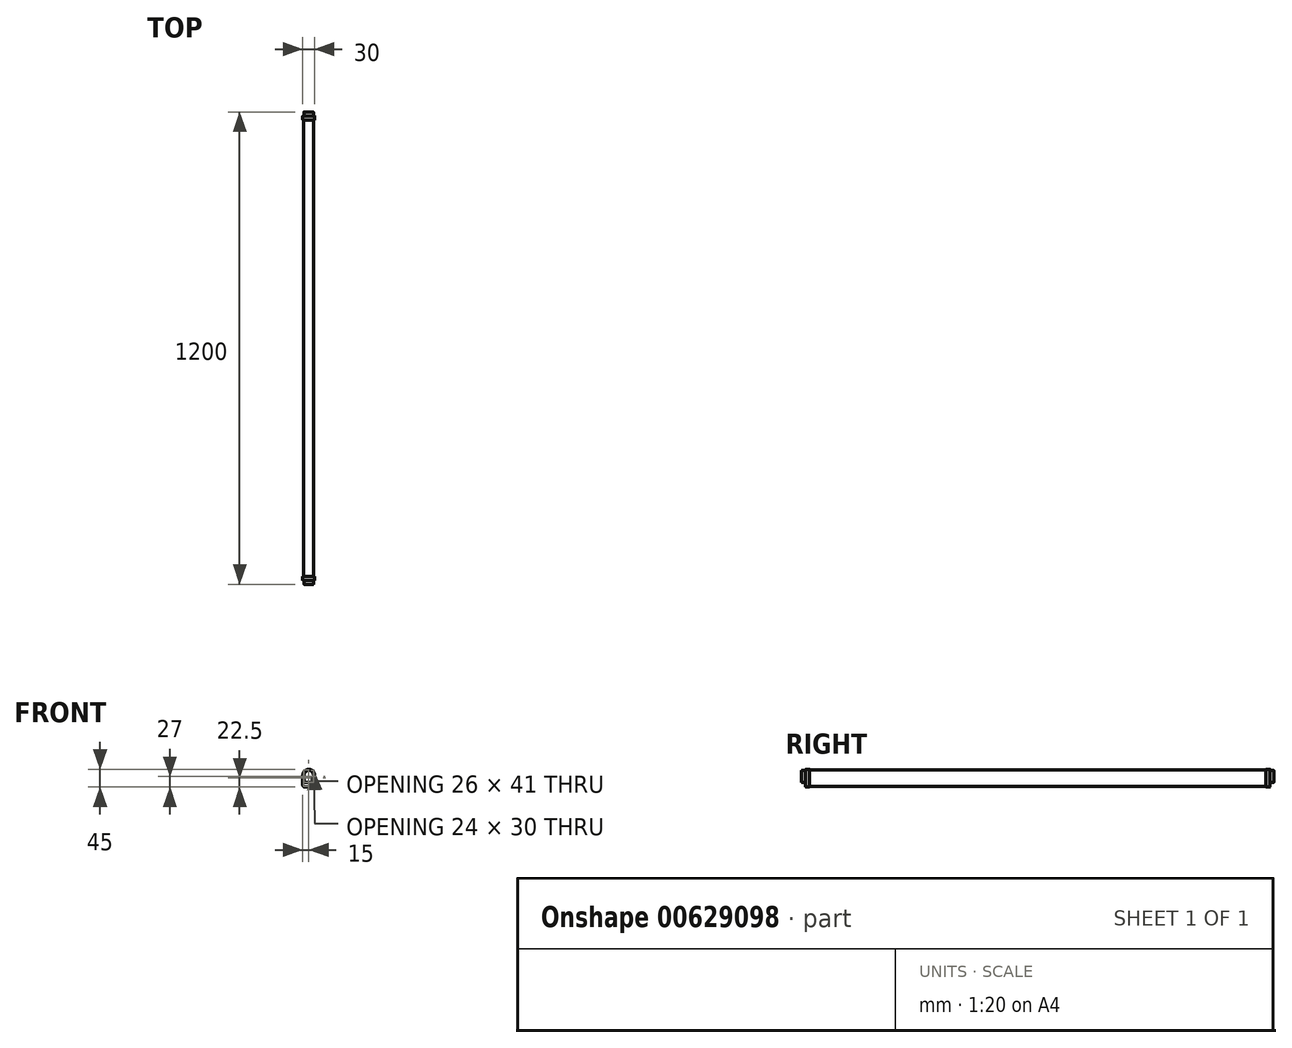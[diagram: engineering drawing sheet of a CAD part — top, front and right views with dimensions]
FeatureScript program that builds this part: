
annotation { "Feature Type Name" : "Feature", "Feature Type Description" : "" }
export const myFeature = defineFeature(function(context is Context, id is Id, definition is map)
    precondition{}
    {
        {
            var Q0;
            Q0=qCreatedBy(makeId("Front.planeOp"),FACE);
            var sketch = newSketch(context, id + "F0", { "sketchPlane" : qUnion([Q0])});
            skLineSegment(sketch, "E0.bottom", {"start": v(10, -22.5) * mm, "end": v(-10, -22.5) * mm});
            skLineSegment(sketch, "E0.top", {"start": v(0, 22.5) * mm, "end": v(0, 22.5) * mm});
            skLineSegment(sketch, "E0.left", {"start": v(15, -17.5) * mm, "end": v(15, 7.5) * mm});
            skLineSegment(sketch, "E0.right", {"start": v(-15, -17.5) * mm, "end": v(-15, 7.5) * mm});
            skPoint(sketch, "E0.middle", {"position": v(0, 0) * mm});
            skPoint(sketch, "E1.visualSharp", {"position": v(-15, 22.5) * mm});
            skArc(sketch, "E1.filletArc", {"start": v(0, 22.5) * mm, "mid": v(-10.6, 18.1) * mm, "end": v(-15, 7.5) * mm});
            skPoint(sketch, "E2.visualSharp", {"position": v(15, 22.5) * mm});
            skArc(sketch, "E2.filletArc", {"start": v(15, 7.5) * mm, "mid": v(10.6, 18.1) * mm, "end": v(0, 22.5) * mm});
            skPoint(sketch, "E3.visualSharp", {"position": v(-15, -22.5) * mm});
            skArc(sketch, "E3.filletArc", {"start": v(-15, -17.5) * mm, "mid": v(-13.54, -21.04) * mm, "end": v(-10, -22.5) * mm});
            skPoint(sketch, "E4.visualSharp", {"position": v(15, -22.5) * mm});
            skArc(sketch, "E4.filletArc", {"start": v(10, -22.5) * mm, "mid": v(13.54, -21.04) * mm, "end": v(15, -17.5) * mm});
            skArc(sketch, "E5.1", {"start": v(12, 7.5) * mm, "mid": v(8.49, 15.99) * mm, "end": v(0, 19.5) * mm});
            skArc(sketch, "E5.2", {"start": v(0, 19.5) * mm, "mid": v(-8.49, 15.99) * mm, "end": v(-12, 7.5) * mm});
            skPoint(sketch, "E6", {"position": v(0, -10.5) * mm});
            skLineSegment(sketch, "E7", {"start": v(0, -10.5) * mm, "end": v(12, -10.5) * mm});
            skLineSegment(sketch, "E8", {"start": v(0, -10.5) * mm, "end": v(-12, -10.5) * mm});
            skLineSegment(sketch, "E9", {"start": v(12, -10.5) * mm, "end": v(12, 7.5) * mm});
            skLineSegment(sketch, "E10", {"start": v(-12, -10.5) * mm, "end": v(-12, 7.5) * mm});
            skArc(sketch, "E11.0", {"start": v(13, 7.5) * mm, "mid": v(9.2, 16.7) * mm, "end": v(0, 20.5) * mm});
            skLineSegment(sketch, "E11.1", {"start": v(13, -17.5) * mm, "end": v(13, 7.5) * mm});
            skLineSegment(sketch, "E11.2", {"start": v(-13, -17.5) * mm, "end": v(-13, 7.5) * mm});
            skArc(sketch, "E11.3", {"start": v(-13, -17.5) * mm, "mid": v(-12.12, -19.62) * mm, "end": v(-10, -20.5) * mm});
            skLineSegment(sketch, "E11.4", {"start": v(10, -20.5) * mm, "end": v(-10, -20.5) * mm});
            skArc(sketch, "E11.5", {"start": v(0, 20.5) * mm, "mid": v(-9.2, 16.7) * mm, "end": v(-13, 7.5) * mm});
            skArc(sketch, "E11.6", {"start": v(10, -20.5) * mm, "mid": v(12.12, -19.62) * mm, "end": v(13, -17.5) * mm});
            skSolve(sketch);
        }
        {
            var Q0;
            Q0=makeQuery(id+"F0.imprint","IMPRINT",FACE,{"disambiguationData":[TD([[makeQuery(id+"F0.imprint","IMPRINT",EDGE,{"derivedFrom":sQuery(id+"F0.wireOp",EDGE,"E5.1")}),-1.0]])]});
            var Q1;
            Q1=makeQuery(id+"F0.imprint","IMPRINT",FACE,{"disambiguationData":[TD([[makeQuery(id+"F0.imprint","IMPRINT",EDGE,{"derivedFrom":sQuery(id+"F0.wireOp",EDGE,"E5.1")}),1.0]])]});
            extrude(context, id + "F1", {"entities" : qUnion([Q0, Q1]), "depth" : 580 * mm, "offsetDistance" : 25 * mm});
        }
        {
            var Q0;
            Q0=makeQuery(id+"F1.opExtrude","CAP_FACE",FACE,{"disambiguationData":[OSD([sQuery(id+"F0.wireOp",EDGE,"E11.0"),sQuery(id+"F0.wireOp",EDGE,"E11.1"),sQuery(id+"F0.wireOp",EDGE,"E11.2"),sQuery(id+"F0.wireOp",EDGE,"E11.3"),sQuery(id+"F0.wireOp",EDGE,"E11.4"),sQuery(id+"F0.wireOp",EDGE,"E11.5"),sQuery(id+"F0.wireOp",EDGE,"E11.6")])],"isStart":false});
            var sketch = newSketch(context, id + "F2", { "sketchPlane" : qUnion([Q0])});
            skLineSegment(sketch, "E12.0.0", {"start": v(15, -17.5) * mm, "end": v(15, 7.5) * mm});
            skArc(sketch, "E12.0.1", {"start": v(15, 7.5) * mm, "mid": v(10.6, 18.1) * mm, "end": v(0, 22.5) * mm});
            skArc(sketch, "E12.0.2", {"start": v(0, 22.5) * mm, "mid": v(-10.6, 18.1) * mm, "end": v(-15, 7.5) * mm});
            skLineSegment(sketch, "E12.0.3", {"start": v(-15, 7.5) * mm, "end": v(-15, -17.5) * mm});
            skArc(sketch, "E12.0.4", {"start": v(-15, -17.5) * mm, "mid": v(-13.54, -21.04) * mm, "end": v(-10, -22.5) * mm});
            skLineSegment(sketch, "E12.0.5", {"start": v(-10, -22.5) * mm, "end": v(10, -22.5) * mm});
            skArc(sketch, "E12.0.6", {"start": v(10, -22.5) * mm, "mid": v(13.54, -21.04) * mm, "end": v(15, -17.5) * mm});
            skSolve(sketch);
        }
        {
            var Q0;
            Q0=qSketchRegion(id+"F2",true);
            extrude(context, id + "F3", {"entities" : qUnion([Q0]), "depth" : 10 * mm, "offsetDistance" : 25 * mm});
        }
        {
            var Q0;
            Q0=makeQuery(id+"F3.opExtrude","CAP_FACE",FACE,{"disambiguationData":[OSD([sQuery(id+"F2.wireOp",EDGE,"E12.0.0"),sQuery(id+"F2.wireOp",EDGE,"E12.0.1"),sQuery(id+"F2.wireOp",EDGE,"E12.0.2"),sQuery(id+"F2.wireOp",EDGE,"E12.0.3"),sQuery(id+"F2.wireOp",EDGE,"E12.0.4"),sQuery(id+"F2.wireOp",EDGE,"E12.0.5"),sQuery(id+"F2.wireOp",EDGE,"E12.0.6")])],"isStart":false});
            var sketch = newSketch(context, id + "F4", { "sketchPlane" : qUnion([Q0])});
            skLineSegment(sketch, "E13.0", {"start": v(-12, -10.5) * mm, "end": v(-12, 7.5) * mm});
            skArc(sketch, "E13.1", {"start": v(0, 19.5) * mm, "mid": v(-8.49, 15.99) * mm, "end": v(-12, 7.5) * mm});
            skArc(sketch, "E13.2", {"start": v(12, 7.5) * mm, "mid": v(8.49, 15.99) * mm, "end": v(0, 19.5) * mm});
            skLineSegment(sketch, "E13.3", {"start": v(12, -10.5) * mm, "end": v(12, 7.5) * mm});
            skLineSegment(sketch, "E13.4", {"start": v(0, -10.5) * mm, "end": v(12, -10.5) * mm});
            skLineSegment(sketch, "E13.5", {"start": v(0, -10.5) * mm, "end": v(-12, -10.5) * mm});
            skSolve(sketch);
        }
        {
            var Q0;
            Q0=qSketchRegion(id+"F4",true);
            extrude(context, id + "F5", {"entities" : qUnion([Q0]), "operationType" : NewBodyOperationType.ADD, "depth" : 10 * mm, "offsetDistance" : 25 * mm});
        }
        {
            var Q0;
            Q0=makeQuery(id+"F5.opExtrude","CAP_EDGE",EDGE,{"disambiguationData":[OSD([sQuery(id+"F4.wireOp",EDGE,"E13.4"),sQuery(id+"F4.wireOp",EDGE,"E13.5")])],"isStart":false});
            var Q1;
            Q1=makeQuery(id+"F5.opExtrude","CAP_EDGE",EDGE,{"disambiguationData":[OSD([sQuery(id+"F4.wireOp",EDGE,"E13.0")])],"isStart":false});
            var Q2;
            Q2=makeQuery(id+"F3.opExtrude","CAP_EDGE",EDGE,{"disambiguationData":[OSD([sQuery(id+"F2.wireOp",EDGE,"E12.0.3")])],"isStart":false});
            var Q3;
            Q3=makeQuery(id+"F3.opExtrude","CAP_EDGE",EDGE,{"disambiguationData":[OSD([sQuery(id+"F2.wireOp",EDGE,"E12.0.1"),sQuery(id+"F2.wireOp",EDGE,"E12.0.2")])],"isStart":false});
            var Q4;
            Q4=makeQuery(id+"F3.opExtrude","CAP_EDGE",EDGE,{"disambiguationData":[OSD([sQuery(id+"F2.wireOp",EDGE,"E12.0.3")])],"isStart":true});
            fillet(context, id + "F6", {"entities" : qUnion([Q0, Q1, Q2, Q3, Q4]), "radius" : 0.5 * mm, "tangentPropagation" : true, "allowEdgeOverflow" : false});
        }
        {
            var Q0;
            Q0=makeQuery(id+"F1.opExtrude","SWEPT_BODY",BODY,{"disambiguationData":[OSD([sQuery(id+"F0.wireOp",EDGE,"E11.0"),sQuery(id+"F0.wireOp",EDGE,"E11.1"),sQuery(id+"F0.wireOp",EDGE,"E11.2"),sQuery(id+"F0.wireOp",EDGE,"E11.3"),sQuery(id+"F0.wireOp",EDGE,"E11.4"),sQuery(id+"F0.wireOp",EDGE,"E11.5"),sQuery(id+"F0.wireOp",EDGE,"E11.6")])]});
            var Q1;
            Q1=qCreatedBy(makeId("Front.planeOp"),FACE);
            mirror(context, id + "F7", {"operationType" : NewBodyOperationType.ADD, "entities" : qUnion([Q0]), "mirrorPlane" : qUnion([Q1])});
        }
        {
            var Q0;
            Q0=makeQuery(id+"F3.opExtrude","SWEPT_BODY",BODY,{"disambiguationData":[OSD([sQuery(id+"F2.wireOp",EDGE,"E12.0.0"),sQuery(id+"F2.wireOp",EDGE,"E12.0.1"),sQuery(id+"F2.wireOp",EDGE,"E12.0.2"),sQuery(id+"F2.wireOp",EDGE,"E12.0.3"),sQuery(id+"F2.wireOp",EDGE,"E12.0.4"),sQuery(id+"F2.wireOp",EDGE,"E12.0.5"),sQuery(id+"F2.wireOp",EDGE,"E12.0.6")])]});
            var Q1;
            Q1=qCreatedBy(makeId("Front.planeOp"),FACE);
            mirror(context, id + "F8", {"entities" : qUnion([Q0]), "mirrorPlane" : qUnion([Q1])});
        }
    });
